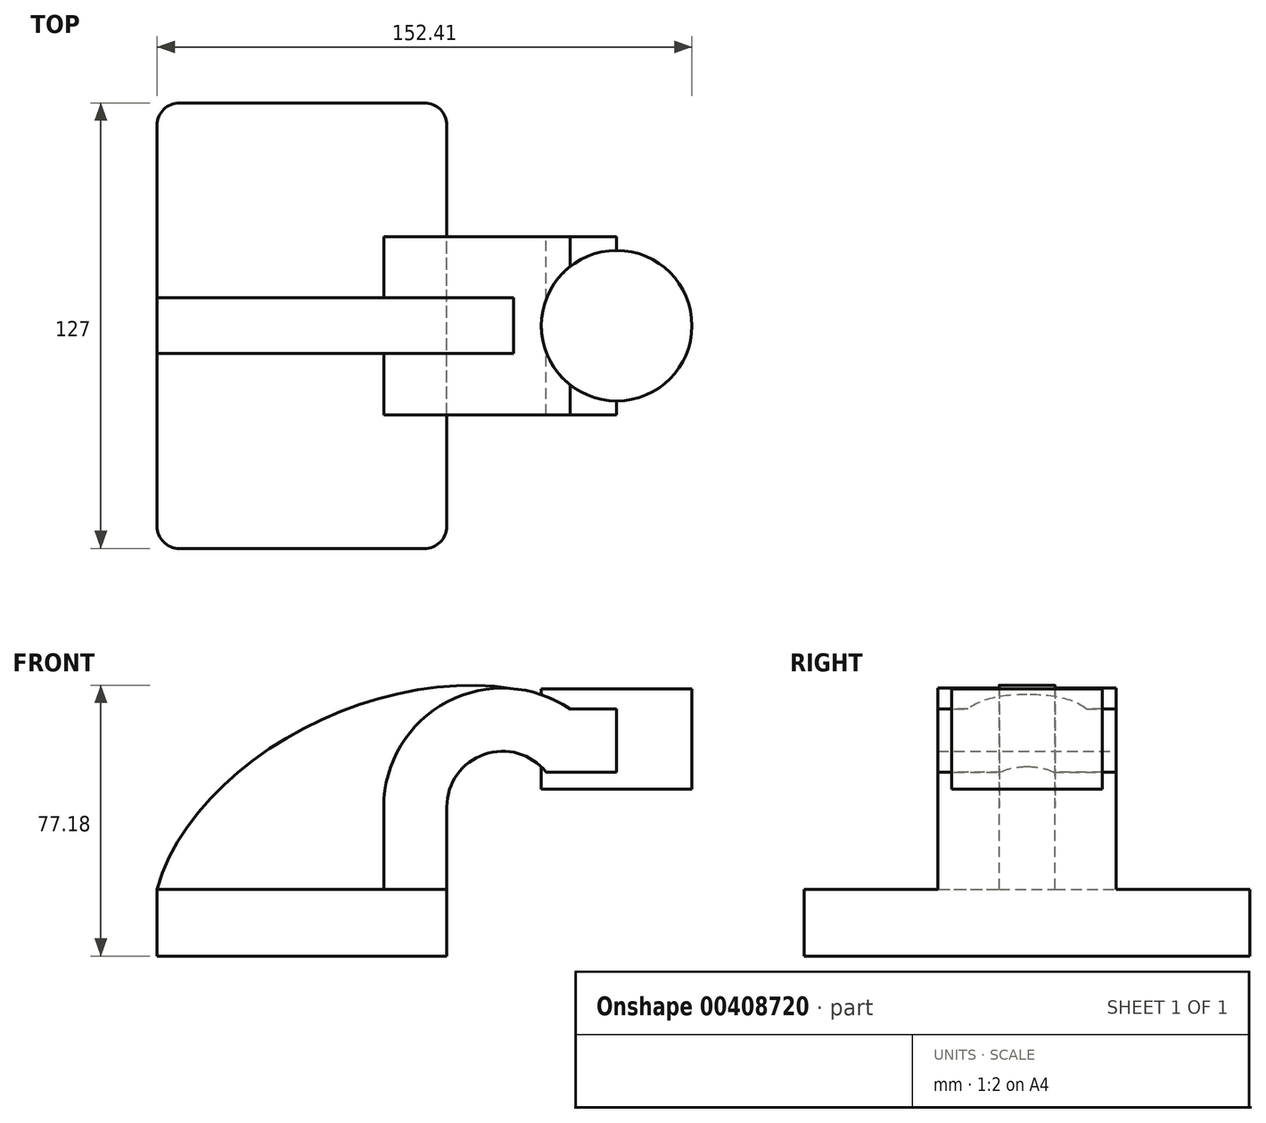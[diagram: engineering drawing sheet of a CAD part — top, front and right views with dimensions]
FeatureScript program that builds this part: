
annotation { "Feature Type Name" : "Feature", "Feature Type Description" : "" }
export const myFeature = defineFeature(function(context is Context, id is Id, definition is map)
    precondition{}
    {
        {
            var Q0;
            Q0=qCreatedBy(makeId("Front.planeOp"),FACE);
            var sketch = newSketch(context, id + "F0", { "sketchPlane" : qUnion([Q0])});
            skLineSegment(sketch, "E0.bottom", {"start": v(-41.27, -9.53) * mm, "end": v(41.28, -9.53) * mm});
            skLineSegment(sketch, "E0.top", {"start": v(-41.28, 9.53) * mm, "end": v(41.28, 9.53) * mm});
            skLineSegment(sketch, "E0.left", {"start": v(-41.28, -9.53) * mm, "end": v(-41.28, 9.53) * mm});
            skLineSegment(sketch, "E0.right", {"start": v(41.28, -9.53) * mm, "end": v(41.28, 9.52) * mm});
            skPoint(sketch, "E0.middle", {"position": v(0, 0) * mm});
            skLineSegment(sketch, "E1.bottom", {"start": v(60.32, 66.67) * mm, "end": v(111.12, 66.67) * mm});
            skLineSegment(sketch, "E1.top", {"start": v(60.32, 38.1) * mm, "end": v(111.12, 38.1) * mm});
            skLineSegment(sketch, "E1.left", {"start": v(60.32, 66.67) * mm, "end": v(60.32, 38.1) * mm});
            skLineSegment(sketch, "E1.right", {"start": v(111.12, 66.67) * mm, "end": v(111.12, 38.1) * mm});
            skPoint(sketch, "E1.middle", {"position": v(85.72, 52.39) * mm});
            skLineSegment(sketch, "E2", {"start": v(41.28, 9.52) * mm, "end": v(41.28, 32.98) * mm});
            skArc(sketch, "E3", {"start": v(41.27, 32.98) * mm, "mid": v(51.9, 47.96) * mm, "end": v(69.56, 42.88) * mm});
            skLineSegment(sketch, "E4", {"start": v(69.56, 42.88) * mm, "end": v(89.67, 42.88) * mm});
            skLineSegment(sketch, "E5.0", {"start": v(47.63, 9.52) * mm, "end": v(47.63, 29.04) * mm});
            skLineSegment(sketch, "E6.0", {"start": v(76.36, 60.85) * mm, "end": v(89.67, 60.85) * mm});
            skArc(sketch, "E6.1", {"start": v(23.3, 32.98) * mm, "mid": v(41.41, 62.94) * mm, "end": v(76.36, 60.85) * mm});
            skLineSegment(sketch, "E6.2", {"start": v(23.3, 9.52) * mm, "end": v(23.3, 32.98) * mm});
            skLineSegment(sketch, "E7", {"start": v(89.67, 38.1) * mm, "end": v(89.67, 66.67) * mm});
            skFitSpline(sketch, "E8", {"points": [v(-41.27, 9.52) * mm, v(60.32, 66.67) * mm], "startDerivative": vector(29.2, 107.07) * mm, "endDerivative": vector(121.43, -19.9) * mm});
            skSolve(sketch);
        }
        {
            var Q0;
            Q0=makeQuery(id+"F0.imprint","IMPRINT",FACE,{"disambiguationData":[TD([[makeQuery(id+"F0.imprint","IMPRINT",EDGE,{"derivedFrom":sQuery(id+"F0.wireOp",EDGE,"E0.bottom")}),1.0]])]});
            extrude(context, id + "F1", {"entities" : qUnion([Q0]), "depth" : 127 * mm, "symmetric" : true});
        }
        {
            var Q0;
            {var subQ1=sQuery(id+"F0.wireOp",EDGE,"E2");Q0=makeQuery(id+"F0.imprint","IMPRINT",FACE,{"disambiguationData":[TD([[makeQuery(id+"F0.imprint","IMPRINT",EDGE,{"derivedFrom":subQ1}),1.0]])]});}
            var Q1;
            {var subQ1=sQuery(id+"F0.wireOp",EDGE,"E4");Q1=makeQuery(id+"F0.imprint","IMPRINT",FACE,{"disambiguationData":[TD([[makeQuery(id+"F0.imprint","IMPRINT",EDGE,{"derivedFrom":subQ1}),1.0]])]});}
            extrude(context, id + "F2", {"entities" : qUnion([Q0, Q1]), "operationType" : NewBodyOperationType.ADD, "depth" : 50.8 * mm, "symmetric" : true});
        }
        {
            var Q0;
            {var subQ2=sQuery(id+"F0.wireOp",EDGE,"E6.2");Q0=makeQuery(id+"F0.imprint","IMPRINT",FACE,{"disambiguationData":[TD([[makeQuery(id+"F0.imprint","IMPRINT",EDGE,{"derivedFrom":subQ2}),1.0]])]});}
            extrude(context, id + "F3", {"entities" : qUnion([Q0]), "operationType" : NewBodyOperationType.ADD, "depth" : 15.88 * mm, "symmetric" : true});
        }
        {
            var Q0;
            {var subQ4=sQuery(id+"F0.wireOp",EDGE,"E1.right");Q0=makeQuery(id+"F0.imprint","IMPRINT",FACE,{"disambiguationData":[TD([[makeQuery(id+"F0.imprint","IMPRINT",EDGE,{"derivedFrom":subQ4}),-1.0]])]});}
            var Q1;
            Q1=sQuery(id+"F0.wireOp",EDGE,"E7");
            revolve(context, id + "F4", {"operationType" : NewBodyOperationType.ADD, "entities" : qUnion([Q0]), "axis" : qUnion([Q1]), "revolveType" : RevolveType.FULL});
        }
        {
            var Q0;
            Q0=makeQuery(id+"F1.opExtrude","CAP_EDGE",EDGE,{"disambiguationData":[OSD([sQuery(id+"F0.wireOp",EDGE,"E0.left")])],"isStart":false});
            var Q1;
            Q1=makeQuery(id+"F1.opExtrude","CAP_EDGE",EDGE,{"disambiguationData":[OSD([sQuery(id+"F0.wireOp",EDGE,"E0.right")])],"isStart":false});
            var Q2;
            Q2=makeQuery(id+"F1.opExtrude","CAP_EDGE",EDGE,{"disambiguationData":[OSD([sQuery(id+"F0.wireOp",EDGE,"E0.left")])],"isStart":true});
            var Q3;
            Q3=makeQuery(id+"F1.opExtrude","CAP_EDGE",EDGE,{"disambiguationData":[OSD([sQuery(id+"F0.wireOp",EDGE,"E0.right")])],"isStart":true});
            fillet(context, id + "F5", {"entities" : qUnion([Q0, Q1, Q2, Q3]), "radius" : 6.35 * mm, "tangentPropagation" : true, "allowEdgeOverflow" : false});
        }
    });
